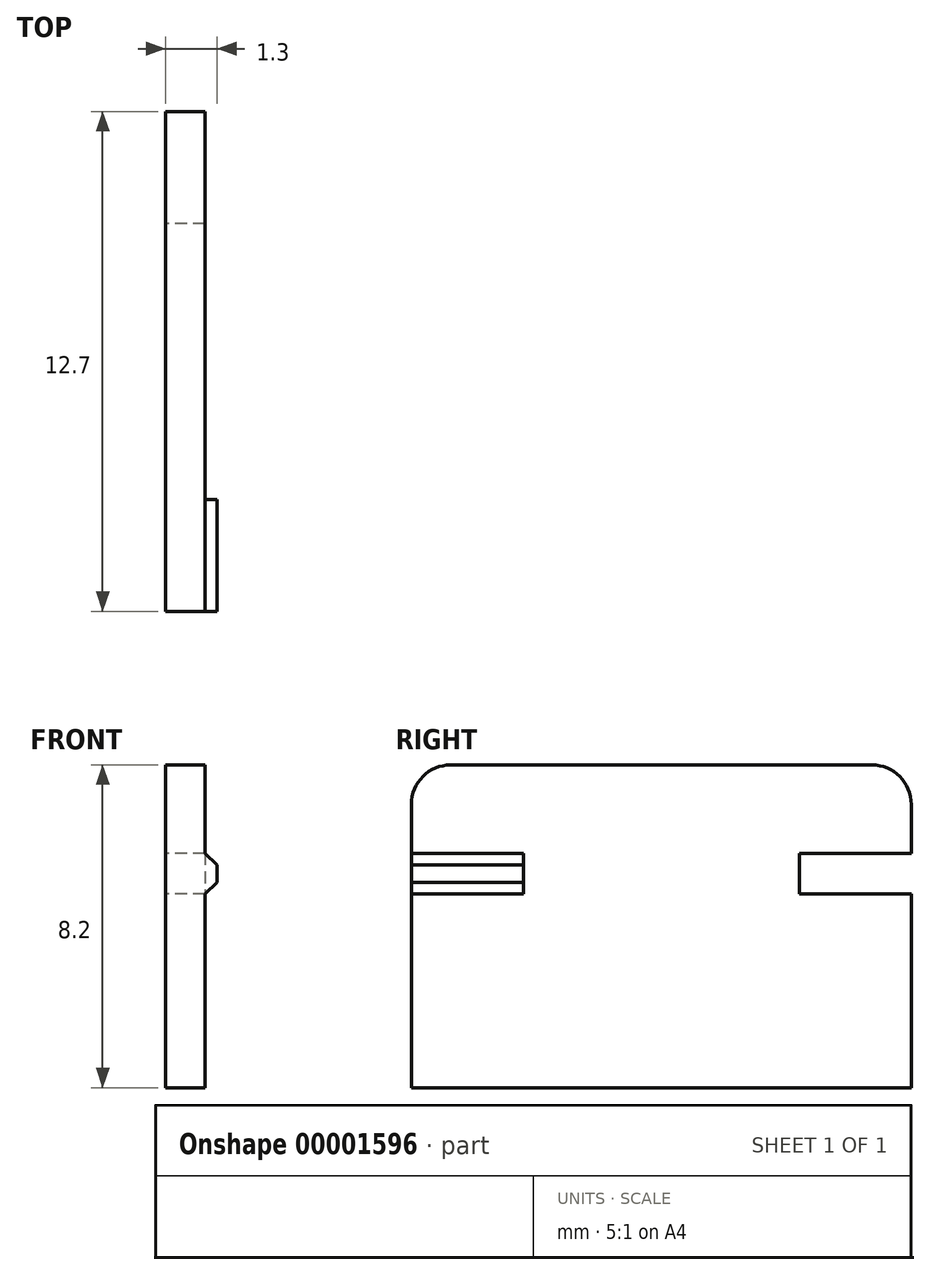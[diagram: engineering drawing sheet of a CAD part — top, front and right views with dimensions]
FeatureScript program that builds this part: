
annotation { "Feature Type Name" : "Feature", "Feature Type Description" : "" }
export const myFeature = defineFeature(function(context is Context, id is Id, definition is map)
    precondition{}
    {
        {
            var Q0;
            Q0=qCreatedBy(makeId("Right.planeOp"),FACE);
            var sketch = newSketch(context, id + "F0", { "sketchPlane" : qUnion([Q0])});
            skLineSegment(sketch, "E0.bottom", {"start": v(-6.35, 4.1) * mm, "end": v(6.35, 4.1) * mm});
            skLineSegment(sketch, "E0.top", {"start": v(-6.35, -4.1) * mm, "end": v(6.35, -4.1) * mm});
            skLineSegment(sketch, "E0.left", {"start": v(-6.35, 4.1) * mm, "end": v(-6.35, -4.1) * mm});
            skLineSegment(sketch, "E0.right", {"start": v(6.35, 4.1) * mm, "end": v(6.35, -4.1) * mm});
            skLineSegment(sketch, "E1.bottom", {"start": v(-6.35, 1.86) * mm, "end": v(-3.5, 1.86) * mm});
            skLineSegment(sketch, "E1.top", {"start": v(-6.35, 0.82) * mm, "end": v(-3.5, 0.82) * mm});
            skLineSegment(sketch, "E1.left", {"start": v(-6.35, 1.86) * mm, "end": v(-6.35, 0.82) * mm});
            skLineSegment(sketch, "E1.right", {"start": v(-3.5, 1.86) * mm, "end": v(-3.5, 0.82) * mm});
            skLineSegment(sketch, "E2", {"start": v(0, 10.16) * mm, "end": v(0, -7.99) * mm, "construction": true});
            skPoint(sketch, "E2.startSnap0", {"position": v(0, 4.1) * mm});
            skLineSegment(sketch, "E3.MirrorCS", {"start": v(6.35, 1.86) * mm, "end": v(6.35, 0.82) * mm});
            skLineSegment(sketch, "E4.MirrorCS", {"start": v(3.5, 1.86) * mm, "end": v(3.5, 0.82) * mm});
            skLineSegment(sketch, "E5.MirrorCS", {"start": v(6.35, 1.86) * mm, "end": v(3.5, 1.86) * mm});
            skLineSegment(sketch, "E6.MirrorCS", {"start": v(6.35, 0.82) * mm, "end": v(3.5, 0.82) * mm});
            skSolve(sketch);
        }
        {
            var Q0;
            {var subQ1=sQuery(id+"F0.wireOp",EDGE,"E0.bottom");Q0=makeQuery(id+"F0.imprint","IMPRINT",FACE,{"disambiguationData":[TD([[makeQuery(id+"F0.imprint","IMPRINT",EDGE,{"derivedFrom":subQ1}),-1.0]])]});}
            extrude(context, id + "F1", {"entities" : qUnion([Q0]), "depth" : 1 * mm});
        }
        {
            var Q0;
            Q0=makeQuery(id+"F0.imprint","IMPRINT",FACE,{"disambiguationData":[TD([[makeQuery(id+"F0.imprint","IMPRINT",EDGE,{"derivedFrom":sQuery(id+"F0.wireOp",EDGE,"E1.bottom")}),-1.0]])]});
            var Q1;
            Q1=makeQuery(id+"F0.imprint","IMPRINT",FACE,{"disambiguationData":[TD([[makeQuery(id+"F0.imprint","IMPRINT",EDGE,{"derivedFrom":sQuery(id+"F0.wireOp",EDGE,"E3.MirrorCS")}),-1.0]])]});
            extrude(context, id + "F2", {"entities" : qUnion([Q0, Q1]), "operationType" : NewBodyOperationType.ADD, "depth" : 1.3 * mm});
        }
        {
            var Q0;
            Q0=makeQuery(id+"F2.opExtrude","CAP_EDGE",EDGE,{"disambiguationData":[OSD([sQuery(id+"F0.wireOp",EDGE,"E1.top")])],"isStart":false});
            var Q1;
            Q1=makeQuery(id+"F2.opExtrude","CAP_EDGE",EDGE,{"disambiguationData":[OSD([sQuery(id+"F0.wireOp",EDGE,"E1.bottom")])],"isStart":false});
            var Q2;
            Q2=makeQuery(id+"F2.opExtrude","CAP_EDGE",EDGE,{"disambiguationData":[OSD([sQuery(id+"F0.wireOp",EDGE,"E6.MirrorCS")])],"isStart":false});
            var Q3;
            Q3=makeQuery(id+"F2.opExtrude","CAP_EDGE",EDGE,{"disambiguationData":[OSD([sQuery(id+"F0.wireOp",EDGE,"E5.MirrorCS")])],"isStart":false});
            chamfer(context, id + "F3", {"entities" : qUnion([Q0, Q1, Q2, Q3]), "width" : 0.3 * mm, "tangentPropagation" : true});
        }
        {
            var Q0;
            Q0=makeQuery(id+"F1.opExtrude","SWEPT_EDGE",EDGE,{"disambiguationData":[OSD([sQuery(id+"F0.wireOp",EDGE,"E0.bottom"),sQuery(id+"F0.wireOp",EDGE,"E0.left")])]});
            var Q1;
            Q1=makeQuery(id+"F1.opExtrude","SWEPT_EDGE",EDGE,{"disambiguationData":[OSD([sQuery(id+"F0.wireOp",EDGE,"E0.bottom"),sQuery(id+"F0.wireOp",EDGE,"E0.right")])]});
            fillet(context, id + "F4", {"entities" : qUnion([Q0, Q1]), "radius" : 1 * mm, "tangentPropagation" : true, "allowEdgeOverflow" : false});
        }
        {
            var Q0;
            Q0=makeQuery(id+"F1.opExtrude","SWEPT_BODY",BODY,{"disambiguationData":[OSD([sQuery(id+"F0.wireOp",EDGE,"E0.bottom"),sQuery(id+"F0.wireOp",EDGE,"E0.top"),sQuery(id+"F0.wireOp",EDGE,"E0.left"),sQuery(id+"F0.wireOp",EDGE,"E0.right"),sQuery(id+"F0.wireOp",EDGE,"E1.bottom"),sQuery(id+"F0.wireOp",EDGE,"E1.top"),sQuery(id+"F0.wireOp",EDGE,"E1.right"),sQuery(id+"F0.wireOp",EDGE,"E4.MirrorCS"),sQuery(id+"F0.wireOp",EDGE,"E5.MirrorCS"),sQuery(id+"F0.wireOp",EDGE,"E6.MirrorCS")])]});
            transform(context, id + "F5", {"entities" : qUnion([Q0]), "transformType" : TransformType.TRANSLATION_3D, "dx" : 0 * mm, "dy" : 0 * mm, "dz" : 0 * mm, "makeCopy" : true});
        }
        {
            var Q0;
            Q0=makeQuery(id+"F5.opPattern","COPY",BODY,{"derivedFrom":makeQuery(id+"F1.opExtrude","SWEPT_BODY",BODY,{"disambiguationData":[OSD([sQuery(id+"F0.wireOp",EDGE,"E0.bottom"),sQuery(id+"F0.wireOp",EDGE,"E0.top"),sQuery(id+"F0.wireOp",EDGE,"E0.left"),sQuery(id+"F0.wireOp",EDGE,"E0.right"),sQuery(id+"F0.wireOp",EDGE,"E1.bottom"),sQuery(id+"F0.wireOp",EDGE,"E1.top"),sQuery(id+"F0.wireOp",EDGE,"E1.right"),sQuery(id+"F0.wireOp",EDGE,"E4.MirrorCS"),sQuery(id+"F0.wireOp",EDGE,"E5.MirrorCS"),sQuery(id+"F0.wireOp",EDGE,"E6.MirrorCS")])]}),"instanceName":"1"});
            deleteBodies(context, id + "F6", {"entities" : qUnion([Q0])});
        }
    });
